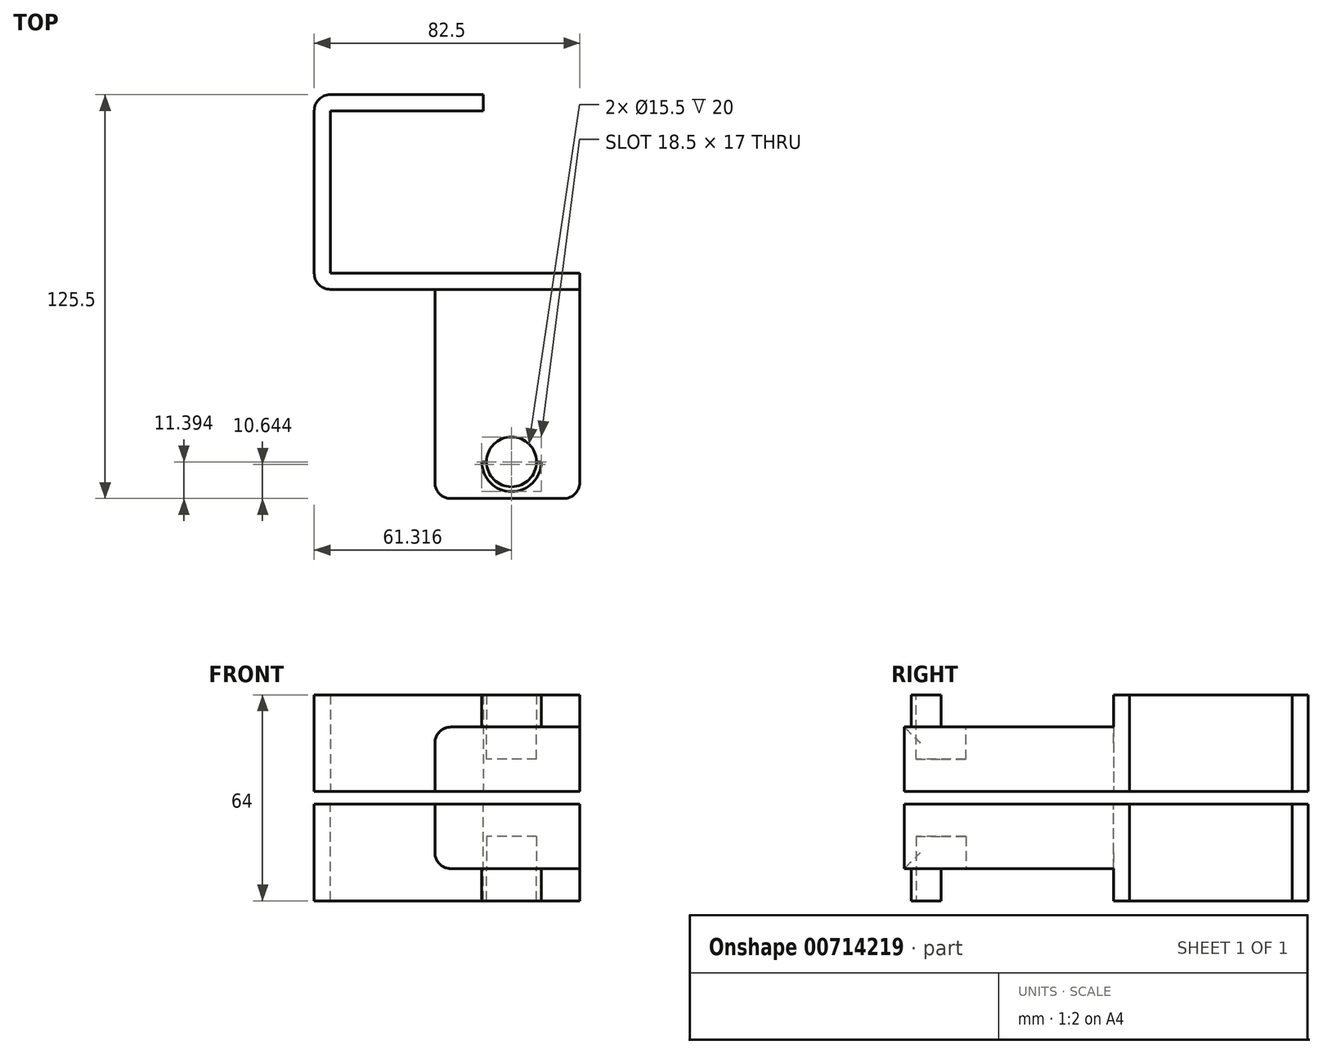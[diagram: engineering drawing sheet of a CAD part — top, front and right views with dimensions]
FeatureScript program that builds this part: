
annotation { "Feature Type Name" : "Feature", "Feature Type Description" : "" }
export const myFeature = defineFeature(function(context is Context, id is Id, definition is map)
    precondition{}
    {
        {
            var Q0;
            Q0=qCreatedBy(makeId("Top.planeOp"),FACE);
            var sketch = newSketch(context, id + "F0", { "sketchPlane" : qUnion([Q0])});
            skLineSegment(sketch, "E0.bottom", {"start": v(-27.95, 37.05) * mm, "end": v(24.55, 37.05) * mm});
            skLineSegment(sketch, "E0.top", {"start": v(-27.95, -23.45) * mm, "end": v(24.55, -23.45) * mm});
            skLineSegment(sketch, "E0.left", {"start": v(-27.95, 37.05) * mm, "end": v(-27.95, -23.45) * mm});
            skLineSegment(sketch, "E0.right", {"start": v(24.55, 37.05) * mm, "end": v(24.55, -23.45) * mm});
            skLineSegment(sketch, "E1.0", {"start": v(19.55, 32.05) * mm, "end": v(19.55, -18.45) * mm});
            skLineSegment(sketch, "E1.1", {"start": v(-22.95, 32.05) * mm, "end": v(19.55, 32.05) * mm});
            skLineSegment(sketch, "E1.2", {"start": v(-22.95, 32.05) * mm, "end": v(-22.95, -18.45) * mm});
            skLineSegment(sketch, "E1.3", {"start": v(-22.95, -18.45) * mm, "end": v(19.55, -18.45) * mm});
            skLineSegment(sketch, "E2", {"start": v(19.55, 32.05) * mm, "end": v(24.55, 32.05) * mm});
            skLineSegment(sketch, "E3", {"start": v(19.55, -18.45) * mm, "end": v(24.55, -18.45) * mm});
            skSolve(sketch);
        }
        {
            var Q0;
            {var subQ1=sQuery(id+"F0.wireOp",EDGE,"E0.bottom");Q0=makeQuery(id+"F0.imprint","IMPRINT",FACE,{"disambiguationData":[TD([[makeQuery(id+"F0.imprint","IMPRINT",EDGE,{"derivedFrom":subQ1}),-1.0]])]});}
            extrude(context, id + "F1", {"entities" : qUnion([Q0]), "depth" : 30 * mm, "offsetDistance" : 25 * mm});
        }
        {
            var Q0;
            {var subQ0=sQuery(id+"F0.wireOp",EDGE,"E0.right");Q0=makeQuery(id+"F1.opExtrude","SWEPT_FACE",FACE,{"disambiguationData":[OSD([subQ0]),TDD([makeQuery(id+"F0.imprint","IMPRINT",EDGE,{"disambiguationData":[TD([[makeQuery(id+"F0.imprint","INTERSECT",VERTEX,{"derivedFrom":[sQuery(id+"F0.wireOp",EDGE,"E0.top"),subQ0]}),1.0]])],"derivedFrom":subQ0})])]});}
            extrude(context, id + "F2", {"entities" : qUnion([Q0]), "operationType" : NewBodyOperationType.ADD, "depth" : 30 * mm, "offsetDistance" : 25 * mm});
        }
        {
            var Q0;
            {var subQ0=sQuery(id+"F0.wireOp",EDGE,"E0.top");Q0=makeQuery(id+"F2.boolean.opBoolean","MERGE",FACE,{"derivedFrom":[makeQuery(id+"F1.opExtrude","SWEPT_FACE",FACE,{"disambiguationData":[OSD([subQ0])]}),makeQuery(id+"F2.opExtrude","SWEPT_FACE",FACE,{"disambiguationData":[OSD([subQ0,sQuery(id+"F0.wireOp",EDGE,"E0.right")])]})]});}
            var sketch = newSketch(context, id + "F3", { "sketchPlane" : qUnion([Q0])});
            skLineSegment(sketch, "E4.bottom", {"start": v(54.55, 30) * mm, "end": v(9.55, 30) * mm});
            skLineSegment(sketch, "E4.top", {"start": v(54.55, 0) * mm, "end": v(9.55, 0) * mm});
            skLineSegment(sketch, "E4.left", {"start": v(54.55, 30) * mm, "end": v(54.55, 0) * mm});
            skLineSegment(sketch, "E4.right", {"start": v(9.55, 30) * mm, "end": v(9.55, 0) * mm});
            skLineSegment(sketch, "E5", {"start": v(9.55, 20) * mm, "end": v(54.55, 20) * mm});
            skSolve(sketch);
        }
        {
            var Q0;
            {var subQ0=sQuery(id+"F3.wireOp",EDGE,"E4.top");Q0=makeQuery(id+"F3.imprint","IMPRINT",FACE,{"disambiguationData":[TD([[makeQuery(id+"F3.imprint","IMPRINT",EDGE,{"derivedFrom":subQ0}),1.0]])]});}
            extrude(context, id + "F4", {"entities" : qUnion([Q0]), "operationType" : NewBodyOperationType.ADD, "depth" : 65 * mm, "offsetDistance" : 25 * mm});
        }
        {
            var Q0;
            Q0=makeQuery(id+"F1.opExtrude","SWEPT_EDGE",EDGE,{"disambiguationData":[OSD([sQuery(id+"F0.wireOp",EDGE,"E0.top"),sQuery(id+"F0.wireOp",EDGE,"E0.left")])]});
            var Q1;
            Q1=makeQuery(id+"F4.opExtrude","SWEPT_EDGE",EDGE,{"disambiguationData":[OSD([sQuery(id+"F3.wireOp",EDGE,"E4.right"),sQuery(id+"F3.wireOp",EDGE,"E5")])]});
            var Q2;
            Q2=makeQuery(id+"F4.opExtrude","CAP_EDGE",EDGE,{"disambiguationData":[OSD([sQuery(id+"F3.wireOp",EDGE,"E4.right")])],"isStart":false});
            var Q3;
            Q3=makeQuery(id+"F4.opExtrude","CAP_EDGE",EDGE,{"disambiguationData":[OSD([sQuery(id+"F3.wireOp",EDGE,"E4.left")])],"isStart":false});
            var Q4;
            Q4=makeQuery(id+"F1.opExtrude","SWEPT_EDGE",EDGE,{"disambiguationData":[OSD([sQuery(id+"F0.wireOp",EDGE,"E0.bottom"),sQuery(id+"F0.wireOp",EDGE,"E0.left")])]});
            var Q5;
            Q5=makeQuery(id+"F4.opExtrude","CAP_EDGE",EDGE,{"disambiguationData":[OSD([sQuery(id+"F3.wireOp",EDGE,"E4.right")])],"isStart":true});
            fillet(context, id + "F5", {"entities" : qUnion([Q0, Q1, Q2, Q3, Q4, Q5]), "radius" : 5 * mm, "tangentPropagation" : true, "allowEdgeOverflow" : false});
        }
        {
            var Q0;
            Q0=qCreatedBy(makeId("Top.planeOp"),FACE);
            cPlane(context, id + "F6", {"entities" : qUnion([Q0]), "cplaneType" : CPlaneType.OFFSET, "offset" : 2 * mm, "oppositeDirection" : true, "width" : 150 * mm, "height" : 150 * mm});
        }
        {
            var Q0;
            Q0=makeQuery(id+"F1.opExtrude","SWEPT_BODY",BODY,{"disambiguationData":[OSD([sQuery(id+"F0.wireOp",EDGE,"E0.bottom"),sQuery(id+"F0.wireOp",EDGE,"E0.top"),sQuery(id+"F0.wireOp",EDGE,"E0.left"),sQuery(id+"F0.wireOp",EDGE,"E0.right"),sQuery(id+"F0.wireOp",EDGE,"E1.1"),sQuery(id+"F0.wireOp",EDGE,"E1.2"),sQuery(id+"F0.wireOp",EDGE,"E1.3"),sQuery(id+"F0.wireOp",EDGE,"E2"),sQuery(id+"F0.wireOp",EDGE,"E3")])]});
            var Q1;
            Q1=qCreatedBy(id+"F6.planeOp",FACE);
            mirror(context, id + "F7", {"entities" : qUnion([Q0]), "mirrorPlane" : qUnion([Q1])});
        }
        {
            var Q0;
            Q0=makeQuery(id+"F4.opExtrude","SWEPT_FACE",FACE,{"disambiguationData":[OSD([sQuery(id+"F3.wireOp",EDGE,"E5")])]});
            var sketch = newSketch(context, id + "F8", { "sketchPlane" : qUnion([Q0])});
            skCircle(sketch, "E6", {"center": v(33.37, -77.06) * mm, "radius": 7.75 * mm});
            skCircle(sketch, "E7.0", {"center": v(33.37, -77.06) * mm, "radius": 9.25 * mm});
            skLineSegment(sketch, "E8", {"start": v(33.37, -77.06) * mm, "end": v(42.62, -77.06) * mm});
            skLineSegment(sketch, "E9", {"start": v(33.37, -77.06) * mm, "end": v(24.12, -77.06) * mm});
            skSolve(sketch);
        }
        {
            var Q0;
            {var subQ0=sQuery(id+"F8.wireOp",EDGE,"E8");var subQ1=sQuery(id+"F8.wireOp",EDGE,"E6");var subQ2=makeQuery(id+"F8.imprint","INTERSECT",VERTEX,{"derivedFrom":[subQ1,subQ0]});Q0=makeQuery(id+"F8.imprint","IMPRINT",FACE,{"disambiguationData":[TD([[makeQuery(id+"F8.imprint","IMPRINT",EDGE,{"disambiguationData":[TD([[subQ2,-1.0]])],"derivedFrom":subQ1}),1.0]])]});}
            var Q1;
            {var subQ0=sQuery(id+"F8.wireOp",EDGE,"E8");var subQ1=sQuery(id+"F8.wireOp",EDGE,"E6");var subQ2=makeQuery(id+"F8.imprint","INTERSECT",VERTEX,{"derivedFrom":[subQ1,subQ0]});Q1=makeQuery(id+"F8.imprint","IMPRINT",FACE,{"disambiguationData":[TD([[makeQuery(id+"F8.imprint","IMPRINT",EDGE,{"disambiguationData":[TD([[subQ2,1.0]])],"derivedFrom":subQ1}),1.0]])]});}
            extrude(context, id + "F9", {"entities" : qUnion([Q0, Q1]), "operationType" : NewBodyOperationType.REMOVE, "oppositeDirection" : true, "depth" : 10 * mm, "offsetDistance" : 25 * mm});
        }
        {
            var Q0;
            {var subQ0=sQuery(id+"F8.wireOp",EDGE,"E8");var subQ1=sQuery(id+"F8.wireOp",EDGE,"E6");var subQ2=makeQuery(id+"F8.imprint","INTERSECT",VERTEX,{"derivedFrom":[subQ1,subQ0]});Q0=makeQuery(id+"F8.imprint","IMPRINT",FACE,{"disambiguationData":[TD([[makeQuery(id+"F8.imprint","IMPRINT",EDGE,{"disambiguationData":[TD([[subQ2,1.0]])],"derivedFrom":subQ1}),-1.0]])]});}
            extrude(context, id + "F10", {"entities" : qUnion([Q0]), "operationType" : NewBodyOperationType.ADD, "depth" : 10 * mm, "offsetDistance" : 25 * mm});
        }
        {
            var Q0;
            Q0=makeQuery(id+"F7.opPattern","COPY",BODY,{"derivedFrom":makeQuery(id+"F1.opExtrude","SWEPT_BODY",BODY,{"disambiguationData":[OSD([sQuery(id+"F0.wireOp",EDGE,"E0.bottom"),sQuery(id+"F0.wireOp",EDGE,"E0.top"),sQuery(id+"F0.wireOp",EDGE,"E0.left"),sQuery(id+"F0.wireOp",EDGE,"E0.right"),sQuery(id+"F0.wireOp",EDGE,"E1.1"),sQuery(id+"F0.wireOp",EDGE,"E1.2"),sQuery(id+"F0.wireOp",EDGE,"E1.3"),sQuery(id+"F0.wireOp",EDGE,"E2"),sQuery(id+"F0.wireOp",EDGE,"E3")])]}),"instanceName":"1"});
            deleteBodies(context, id + "F11", {"entities" : qUnion([Q0])});
        }
        {
            var Q0;
            Q0=makeQuery(id+"F1.opExtrude","SWEPT_BODY",BODY,{"disambiguationData":[OSD([sQuery(id+"F0.wireOp",EDGE,"E0.bottom"),sQuery(id+"F0.wireOp",EDGE,"E0.top"),sQuery(id+"F0.wireOp",EDGE,"E0.left"),sQuery(id+"F0.wireOp",EDGE,"E0.right"),sQuery(id+"F0.wireOp",EDGE,"E1.1"),sQuery(id+"F0.wireOp",EDGE,"E1.2"),sQuery(id+"F0.wireOp",EDGE,"E1.3"),sQuery(id+"F0.wireOp",EDGE,"E2"),sQuery(id+"F0.wireOp",EDGE,"E3")])]});
            var Q1;
            Q1=qCreatedBy(id+"F6.planeOp",FACE);
            mirror(context, id + "F12", {"entities" : qUnion([Q0]), "mirrorPlane" : qUnion([Q1])});
        }
    });
